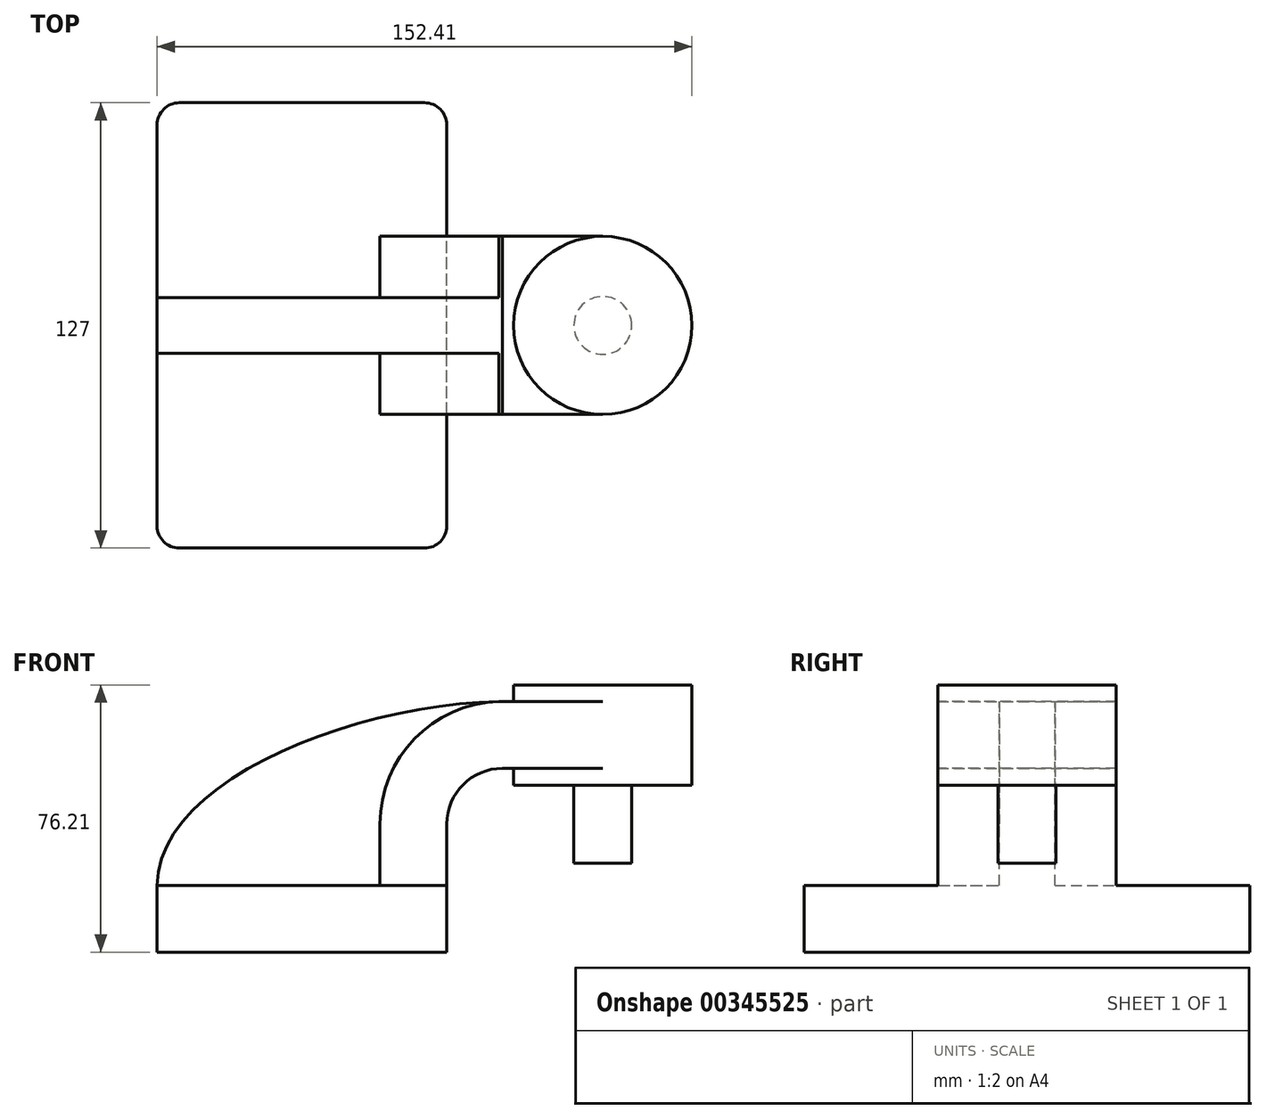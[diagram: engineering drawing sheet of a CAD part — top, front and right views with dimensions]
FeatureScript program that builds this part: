
annotation { "Feature Type Name" : "Feature", "Feature Type Description" : "" }
export const myFeature = defineFeature(function(context is Context, id is Id, definition is map)
    precondition{}
    {
        {
            var Q0;
            Q0=qCreatedBy(makeId("Front.planeOp"),FACE);
            var sketch = newSketch(context, id + "F0", { "sketchPlane" : qUnion([Q0])});
            skLineSegment(sketch, "E0.bottom", {"start": v(41.27, 9.53) * mm, "end": v(-41.28, 9.53) * mm});
            skLineSegment(sketch, "E0.top", {"start": v(41.28, -9.52) * mm, "end": v(-41.27, -9.52) * mm});
            skLineSegment(sketch, "E0.left", {"start": v(41.28, 9.53) * mm, "end": v(41.28, -9.52) * mm});
            skLineSegment(sketch, "E0.right", {"start": v(-41.28, 9.53) * mm, "end": v(-41.27, -9.52) * mm});
            skPoint(sketch, "E0.middle", {"position": v(0, 0) * mm});
            skLineSegment(sketch, "E1.bottom", {"start": v(111.12, 66.68) * mm, "end": v(60.32, 66.68) * mm});
            skLineSegment(sketch, "E1.top", {"start": v(111.12, 38.1) * mm, "end": v(60.32, 38.1) * mm});
            skLineSegment(sketch, "E1.left", {"start": v(111.12, 66.68) * mm, "end": v(111.12, 38.1) * mm});
            skLineSegment(sketch, "E1.right", {"start": v(60.32, 66.68) * mm, "end": v(60.32, 38.1) * mm});
            skPoint(sketch, "E1.middle", {"position": v(85.73, 52.39) * mm});
            skLineSegment(sketch, "E2", {"start": v(41.27, 9.53) * mm, "end": v(41.27, 27) * mm});
            skArc(sketch, "E3", {"start": v(41.27, 27) * mm, "mid": v(45.92, 38.23) * mm, "end": v(57.15, 42.88) * mm});
            skLineSegment(sketch, "E4", {"start": v(57.15, 42.88) * mm, "end": v(85.73, 42.88) * mm});
            skLineSegment(sketch, "E5.0", {"start": v(57.15, 61.93) * mm, "end": v(85.73, 61.93) * mm});
            skArc(sketch, "E5.1", {"start": v(22.22, 27) * mm, "mid": v(32.45, 51.7) * mm, "end": v(57.15, 61.93) * mm});
            skLineSegment(sketch, "E5.2", {"start": v(22.23, 9.53) * mm, "end": v(22.23, 27) * mm});
            skLineSegment(sketch, "E6", {"start": v(85.72, 38.1) * mm, "end": v(85.72, 66.68) * mm});
            skFitSpline(sketch, "E7", {"points": [v(-41.28, 9.53) * mm, v(57.15, 61.93) * mm], "startDerivative": vector(0.4, 89.54) * mm, "endDerivative": vector(126.48, 1.37) * mm});
            skSolve(sketch);
        }
        {
            var Q0;
            Q0=makeQuery(id+"F0.imprint","IMPRINT",FACE,{"disambiguationData":[TD([[makeQuery(id+"F0.imprint","IMPRINT",EDGE,{"derivedFrom":sQuery(id+"F0.wireOp",EDGE,"E0.top")}),-1.0]])]});
            extrude(context, id + "F1", {"entities" : qUnion([Q0]), "endBound" : BoundingType.SYMMETRIC, "depth" : 127 * mm});
        }
        {
            var Q0;
            {var subQ3=sQuery(id+"F0.wireOp",EDGE,"E5.2");Q0=makeQuery(id+"F0.imprint","IMPRINT",FACE,{"disambiguationData":[TD([[makeQuery(id+"F0.imprint","IMPRINT",EDGE,{"derivedFrom":subQ3}),1.0]])]});}
            extrude(context, id + "F2", {"entities" : qUnion([Q0]), "operationType" : NewBodyOperationType.ADD, "endBound" : BoundingType.SYMMETRIC, "oppositeDirection" : true, "depth" : 15.88 * mm});
        }
        {
            var Q0;
            {var subQ1=sQuery(id+"F0.wireOp",EDGE,"E2");Q0=makeQuery(id+"F0.imprint","IMPRINT",FACE,{"disambiguationData":[TD([[makeQuery(id+"F0.imprint","IMPRINT",EDGE,{"derivedFrom":subQ1}),1.0]])]});}
            var Q1;
            {var subQ0=sQuery(id+"F0.wireOp",EDGE,"E5.0");var subQ1=sQuery(id+"F0.wireOp",EDGE,"E1.right");var subQ2=makeQuery(id+"F0.imprint","INTERSECT",VERTEX,{"derivedFrom":[subQ1,subQ0]});Q1=makeQuery(id+"F0.imprint","IMPRINT",FACE,{"disambiguationData":[TD([[makeQuery(id+"F0.imprint","IMPRINT",EDGE,{"disambiguationData":[TD([[subQ2,-1.0]])],"derivedFrom":subQ1}),1.0]])]});}
            extrude(context, id + "F3", {"entities" : qUnion([Q0, Q1]), "operationType" : NewBodyOperationType.ADD, "endBound" : BoundingType.SYMMETRIC, "depth" : 50.8 * mm});
        }
        {
            var Q0;
            {var subQ0=sQuery(id+"F0.wireOp",EDGE,"E1.left");Q0=makeQuery(id+"F0.imprint","IMPRINT",FACE,{"disambiguationData":[TD([[makeQuery(id+"F0.imprint","IMPRINT",EDGE,{"derivedFrom":subQ0}),-1.0]])]});}
            var Q1;
            Q1=sQuery(id+"F0.wireOp",EDGE,"E6");
            revolve(context, id + "F4", {"operationType" : NewBodyOperationType.ADD, "entities" : qUnion([Q0]), "axis" : qUnion([Q1]), "revolveType" : RevolveType.FULL});
        }
        {
            var Q0;
            Q0=makeQuery(id+"F1.opExtrude","CAP_EDGE",EDGE,{"disambiguationData":[OSD([sQuery(id+"F0.wireOp",EDGE,"E0.right")])],"isStart":false});
            var Q1;
            Q1=makeQuery(id+"F1.opExtrude","CAP_EDGE",EDGE,{"disambiguationData":[OSD([sQuery(id+"F0.wireOp",EDGE,"E0.left")])],"isStart":false});
            var Q2;
            Q2=makeQuery(id+"F1.opExtrude","CAP_EDGE",EDGE,{"disambiguationData":[OSD([sQuery(id+"F0.wireOp",EDGE,"E0.left")])],"isStart":true});
            var Q3;
            Q3=makeQuery(id+"F1.opExtrude","CAP_EDGE",EDGE,{"disambiguationData":[OSD([sQuery(id+"F0.wireOp",EDGE,"E0.right")])],"isStart":true});
            fillet(context, id + "F5", {"entities" : qUnion([Q0, Q1, Q2, Q3]), "radius" : 6.35 * mm, "tangentPropagation" : true, "allowEdgeOverflow" : false});
        }
        {
            var Q0;
            Q0=makeQuery(id+"F4.opRevolve","SWEPT_FACE",FACE,{"disambiguationData":[OSD([sQuery(id+"F0.wireOp",EDGE,"E1.bottom")])]});
            var sketch = newSketch(context, id + "F6", { "sketchPlane" : qUnion([Q0])});
            skCircle(sketch, "E8", {"center": v(85.72, 0) * mm, "radius": 8.25 * mm});
            skSolve(sketch);
        }
        {
            var Q0;
            Q0 = qSketchRegion(id + "F6", true);
            extrude(context, id + "F7", {"entities" : qUnion([Q0]), "operationType" : NewBodyOperationType.ADD, "oppositeDirection" : true, "depth" : 50.8 * mm});
        }
    });
